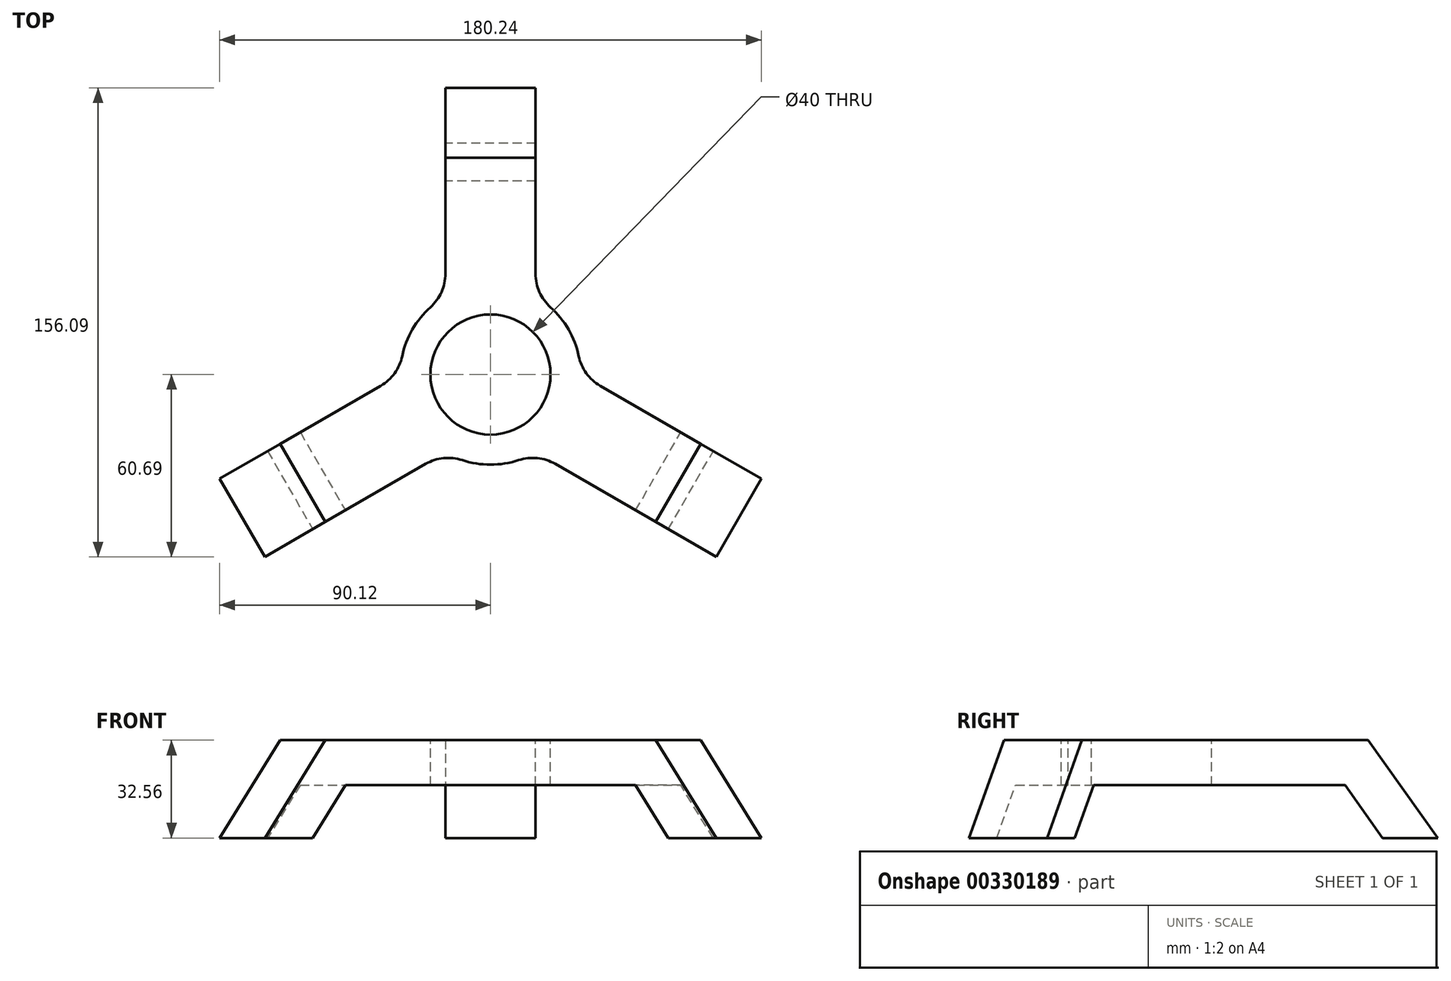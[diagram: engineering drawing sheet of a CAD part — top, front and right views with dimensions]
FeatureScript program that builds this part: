
annotation { "Feature Type Name" : "Feature", "Feature Type Description" : "" }
export const myFeature = defineFeature(function(context is Context, id is Id, definition is map)
    precondition{}
    {
        {
            var Q0;
            Q0=qCreatedBy(makeId("Top.planeOp"),FACE);
            var sketch = newSketch(context, id + "F0", { "sketchPlane" : qUnion([Q0])});
            skCircle(sketch, "E0", {"center": v(0, 0) * mm, "radius": 20 * mm});
            skArc(sketch, "E1", {"start": v(-15, -25.98) * mm, "mid": v(0, -30) * mm, "end": v(15, -25.98) * mm});
            skLineSegment(sketch, "E2", {"start": v(0, 92.5) * mm, "end": v(0, -69.58) * mm, "construction": true});
            skLineSegment(sketch, "E3", {"start": v(-15, 72.17) * mm, "end": v(-15, 25.98) * mm});
            skLineSegment(sketch, "E4.MirrorCS", {"start": v(15, 72.17) * mm, "end": v(15, 25.98) * mm});
            skLineSegment(sketch, "E5", {"start": v(-15, 72.17) * mm, "end": v(15, 72.17) * mm});
            skCircle(sketch, "E6.cCircle", {"center": v(0, 0) * mm, "radius": 144.34 * mm, "construction": true});
            skLineSegment(sketch, "E6.0", {"start": v(-125, 72.17) * mm, "end": v(125, 72.17) * mm, "construction": true});
            skLineSegment(sketch, "E6.1", {"start": v(125, 72.17) * mm, "end": v(0, -144.34) * mm, "construction": true});
            skLineSegment(sketch, "E6.2", {"start": v(0, -144.34) * mm, "end": v(-125, 72.17) * mm, "construction": true});
            skLineSegment(sketch, "E7.1.0", {"start": v(-55, -49.07) * mm, "end": v(-15, -25.98) * mm});
            skLineSegment(sketch, "E7.1.1", {"start": v(-70, -23.1) * mm, "end": v(-30, 0) * mm});
            skLineSegment(sketch, "E7.2.0", {"start": v(70, -23.1) * mm, "end": v(30, 0) * mm});
            skLineSegment(sketch, "E7.2.1", {"start": v(55, -49.07) * mm, "end": v(15, -25.98) * mm});
            skLineSegment(sketch, "E8.1.0", {"start": v(-55, -49.07) * mm, "end": v(-70, -23.1) * mm});
            skLineSegment(sketch, "E8.2.0", {"start": v(70, -23.1) * mm, "end": v(55, -49.07) * mm});
            skArc(sketch, "E9.trimOffspring", {"start": v(30, 0) * mm, "mid": v(25.98, 15) * mm, "end": v(15, 25.98) * mm});
            skArc(sketch, "E10.trimOffspring", {"start": v(-15, 25.98) * mm, "mid": v(-25.98, 15) * mm, "end": v(-30, 0) * mm});
            skSolve(sketch);
        }
        {
            var Q0;
            Q0 = qSketchRegion(id + "F0", true);
            extrude(context, id + "F1", {"entities" : qUnion([Q0]), "oppositeDirection" : true, "depth" : 15 * mm, "offsetDistance" : 25 * mm});
        }
        {
            var Q0;
            Q0=makeQuery(id+"F1.opExtrude","SWEPT_EDGE",EDGE,{"disambiguationData":[OSD([sQuery(id+"F0.wireOp",EDGE,"E3"),sQuery(id+"F0.wireOp",EDGE,"E10.trimOffspring")])]});
            var Q1;
            Q1=makeQuery(id+"F1.opExtrude","SWEPT_EDGE",EDGE,{"disambiguationData":[OSD([sQuery(id+"F0.wireOp",EDGE,"E7.1.1"),sQuery(id+"F0.wireOp",EDGE,"E10.trimOffspring")])]});
            var Q2;
            Q2=makeQuery(id+"F1.opExtrude","SWEPT_EDGE",EDGE,{"disambiguationData":[OSD([sQuery(id+"F0.wireOp",EDGE,"E1"),sQuery(id+"F0.wireOp",EDGE,"E7.1.0")])]});
            var Q3;
            Q3=makeQuery(id+"F1.opExtrude","SWEPT_EDGE",EDGE,{"disambiguationData":[OSD([sQuery(id+"F0.wireOp",EDGE,"E1"),sQuery(id+"F0.wireOp",EDGE,"E7.2.1")])]});
            var Q4;
            Q4=makeQuery(id+"F1.opExtrude","SWEPT_EDGE",EDGE,{"disambiguationData":[OSD([sQuery(id+"F0.wireOp",EDGE,"E4.MirrorCS"),sQuery(id+"F0.wireOp",EDGE,"E9.trimOffspring")])]});
            var Q5;
            Q5=makeQuery(id+"F1.opExtrude","SWEPT_EDGE",EDGE,{"disambiguationData":[OSD([sQuery(id+"F0.wireOp",EDGE,"E7.2.0"),sQuery(id+"F0.wireOp",EDGE,"E9.trimOffspring")])]});
            fillet(context, id + "F2", {"entities" : qUnion([Q0, Q1, Q2, Q3, Q4, Q5]), "radius" : 15 * mm, "tangentPropagation" : true, "allowEdgeOverflow" : false});
        }
        {
            var Q0;
            Q0=makeQuery(id+"F1.opExtrude","SWEPT_FACE",FACE,{"disambiguationData":[OSD([sQuery(id+"F0.wireOp",EDGE,"E7.1.0")])]});
            var sketch = newSketch(context, id + "F3", { "sketchPlane" : qUnion([Q0])});
            skLineSegment(sketch, "E11", {"start": v(-72.17, 0) * mm, "end": v(-95.4, -32.56) * mm});
            skLineSegment(sketch, "E12", {"start": v(-95.4, -32.56) * mm, "end": v(-76.97, -32.56) * mm});
            skLineSegment(sketch, "E13", {"start": v(-76.97, -32.56) * mm, "end": v(-64.44, -15) * mm});
            skLineSegment(sketch, "E14", {"start": v(-72.17, 0) * mm, "end": v(-72.17, -15) * mm});
            skLineSegment(sketch, "E15", {"start": v(-72.17, -15) * mm, "end": v(-64.44, -15) * mm});
            skSolve(sketch);
        }
        {
            var Q0;
            Q0 = qSketchRegion(id + "F3", true);
            var Q1;
            Q1=makeQuery(id+"F1.opExtrude","SWEPT_FACE",FACE,{"disambiguationData":[OSD([sQuery(id+"F0.wireOp",EDGE,"E7.1.1")])]});
            extrude(context, id + "F4", {"entities" : qUnion([Q0]), "endBound" : BoundingType.UP_TO_SURFACE, "oppositeDirection" : true, "depth" : 25 * mm, "endBoundEntityFace" : qUnion([Q1]), "offsetDistance" : 25 * mm});
        }
        {
            var Q0;
            Q0=qCreatedBy(makeId("Front.planeOp"),FACE);
            var sketch = newSketch(context, id + "F5", { "sketchPlane" : qUnion([Q0])});
            skLineSegment(sketch, "E16", {"start": v(0, 62.3) * mm, "end": v(0, -61.14) * mm, "construction": true});
            skSolve(sketch);
        }
        {
            var Q0;
            Q0=makeQuery(id+"F4.opExtrude","SWEPT_BODY",BODY,{"disambiguationData":[OSD([sQuery(id+"F3.wireOp",EDGE,"E11"),sQuery(id+"F3.wireOp",EDGE,"E12"),sQuery(id+"F3.wireOp",EDGE,"E13"),sQuery(id+"F3.wireOp",EDGE,"E14"),sQuery(id+"F3.wireOp",EDGE,"E15")])]});
            var Q1;
            Q1=sQuery(id+"F5.wireOp",EDGE,"E16");
            circularPattern(context, id + "F6", {"operationType" : NewBodyOperationType.ADD, "entities" : qUnion([Q0]), "axis" : qUnion([Q1]), "angle" : 360 * degree, "instanceCount" : 3, "equalSpace" : true});
        }
    });
